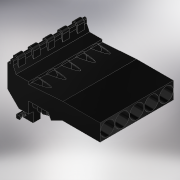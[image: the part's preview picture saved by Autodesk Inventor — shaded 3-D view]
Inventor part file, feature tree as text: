
AUTODESK INVENTOR PART (.ipt)
format: ipt  version: 2018 (Build 220112000, 112)  size: 726,528 bytes
history: native  units: in
note: dims shown in document units (in); Inventor stores cm internally (conversion verified against a paired STEP export)
features: other x15, extrude x15, chamfer x2, fillet x2, pattern_linear x1, sketch x1, projected_geometry x1
ambient origin geometry x8: Origin, YZ Plane, XZ Plane, XY Plane, X Axis, Y Axis, Z Axis, Center Point
bodies: Solid1 (feature_tree)
feature tree (37):
  other  "Base Sketch"
  extrude  "Side Walls"  TaperAngle=0.0deg  [1 undecoded]
  extrude  "Back Wall"  TaperAngle=0.0deg  [1 undecoded]
  extrude  "Front Wall"  TaperAngle=0.0deg  [1 undecoded]
  extrude  "Whistle Housing"  Depth=0.2067in TaperAngle=0.0deg
  extrude  "Tube Socket"  Depth=0.0938in
  other  "Midplane"
  extrude  "Slit"  Depth=0.2067in
  other  "Silicone Fitting"
  extrude  "Silicone Fitting to Chamber"  Depth=0.2067in
  extrude  "Hinge"  Depth=0.2067in
  extrude  "Hinge Nub"  TaperAngle=90.0deg  [1 undecoded]
  chamfer  "Hinge Clearance Chamfer"  Distance=1.5748in
  chamfer  "Spring Pass Chamfer"  Distance=0.4016in
  extrude  "Spring Block"  TaperAngle=0.0deg  [1 undecoded]
  extrude  "Spring Hook"  Depth=0.2067in
  other  "Sping Hook Draft"
  fillet  "Spring Hook Fillet"  Radius=0.4134in
  extrude  "Edge Cut"  TaperAngle=0.0deg  [1 undecoded]
  fillet  "Edge Fillet"  Radius=0.189in
  other  "Pincher Triangle Sketch"
  extrude  "Pincher Triangle"  TaperAngle=0.0deg  [1 undecoded]
  extrude  "Triangle Coupling Male"  Depth=0.2067in
  extrude  "Expand: Triangle Coupling Female"  Depth=0.2067in
  pattern_linear  "Key Repitition"  Spacing1=45.0deg  [1 undecoded]
  sketch  "Sketch5"  dims[d1=0.0in d2=0.0in d3=0.0in d4=0.0in d61=1.5748in d62=0.0in d65=0.0938in d66=0.1181in d67=0.0276in d68=0.0197in d69=90.0deg d71=1.5748in d72=0.0in d78=0.4016in d80=0.0in d81=0.4331in d88=0.4134in d89=0.0in d92=0.189in d93=0.0in d101=0.0079in d105=0.0787in d106=0.1772in d107=45.0deg d112=0.0787in d113=45.0deg d135=0.2067in d136=0.315in d137=0.5906in d139=0.0in d160=0.1181in d161=0.0984in d162=0.3937in d163=0.1575in d164=0.0in d171=1.03in d173=0.4724in d176=0.4134in d177=0.0in d178=0.2067in d179=0.0in d180=0.1374in d181=0.0394in d187=0.2067in d188=0.2362in d190=0.5906in d191=0.0in d193=0.1654in d194=0.0512in d198=0.4134in d199=0.0in d277=0.0079in d278=1.9685in d280=0.4134in d282=0.2067in d283=0.0in d284=0.0394in d285=0.0079in d289=0.0827in d298=0.2067in d299=0.0in d300=0.0787in d301=0.0394in d302=0.0079in d303=0.315in]
  projected_geometry  "Projected Loop2"
  other  "Whistle Housing Sketch"
  other  "Edge Cut Sketch"
  other  "Slit Sketch"
  other  "Silicone Fitting Sketch"
  other  "Silicone Fitting to Chamber Sketch"
  other  "Tube Socket Sketch"
  other  "Hinge Sketch"
  other  "Hinge Nub Sketch"
  other  "Spring Block Sketch"
  other  "Spring Hook Sketch"
note: 8 required parameter values undecoded (feature->parameter linkage not recoverable at this tier; creation-order binding heuristic only, values carry confidence <= 0.55)
